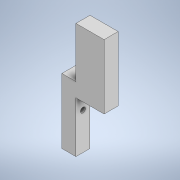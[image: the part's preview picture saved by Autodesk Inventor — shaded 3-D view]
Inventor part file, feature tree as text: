
AUTODESK INVENTOR PART (.ipt)
format: ipt  version: 2020.2 (Build 242310000, 310)  size: 137,728 bytes
history: native  units: mm
features: sketch x6, extrude x5, hole x1, projected_geometry x1
ambient origin geometry x8: Origin, YZ Plane, XZ Plane, XY Plane, X Axis, Y Axis, Z Axis, Center Point
bodies: Solid1 (feature_tree)
feature tree (13):
  extrude  "Extrusion1"  Depth=36.2mm
  hole  "Hole2"  [1 undecoded]
  extrude  "Extrusion2"  Depth=10.0mm TaperAngle=0.0deg
  extrude  "Extrusion3"  Depth=10.0mm
  extrude  "Extrusion4"  Depth=20.0mm TaperAngle=0.0deg
  extrude  "Extrusion5"  [1 undecoded]
  sketch  "Sketch1"  dims[d0=10.0mm d1=36.2mm]
  sketch  "Sketch3"  dims[d2=10.0mm d3=0.0mm d12=10.0mm]
  sketch  "Sketch4"  dims[d13=3.6mm d14=6.0mm d15=6.3mm d16=2.0mm d17=90.0deg d18=8.0mm d19=20.594885mm d20=10.0mm d21=0.0mm]
  sketch  "Sketch5"  dims[d22=10.0mm d23=10.0mm]
  sketch  "Sketch6"  dims[d24=20.0mm d25=0.0mm d26=50.8mm d27=0.0mm]
  sketch  "Sketch7"  dims[d28=15.0mm d29=0.0mm]
  projected_geometry  "Projected Loop1"
note: 2 required parameter values undecoded (feature->parameter linkage not recoverable at this tier; creation-order binding heuristic only, values carry confidence <= 0.55)
